# Revit family: PF_ST_RainTrak- O_ACO_2022
name_source: partatom
category: Plumbing Fixtures
units: mm (PartAtom-declared; Revit-internal decimal feet)

## family parameters
Always vertical = No
Cut with Voids When Loaded = Yes
Maintain Annotation Orientation = No
OmniClass Number = 23.70.50.24
OmniClass Title = Rainwater Removal
Part Type = Normal
Room Calculation Point = No
Round Connector Dimension = Use Diameter
Shared = No
Work Plane-Based = Yes

## types (3) — shared parameters
Default Elevation = 1219 mm
Description = Threshold door drainage
Fax = +61 2 4747 4040
IfcDescription = Threshold door drainage
IfcExportAs = IfcWasteTerminalType
IfcExportType = USERDEFINED
Installation guidelines = http://www.acobuildline.com.au
Maintenance guidelines = http://www.acobuildline.com.au
Manufacturer = ACO Pty Ltd
Model = RainTrak
Product_brochure = http://www.acobuildline.com.au
Product_page_URL = http://www.acobuildline.com.au
Telephone = +61 2 4747 4000
URL = www.acobuildline.com.au
d1 = 38 mm
d2 = 51 mm
d3 = 64 mm
d4 = 76 mm
d5 = 89 mm
d6 = 102 mm
region_index = 1

## per-type parameters (varying)
| type | Assembly Code | type_index |
| RainTrak-O-75mm width | D2040300 | 1 |
| RainTrak-O-100mm width |  | 2 |
| RainTrak-O-123mm width |  | 3 |

## geometry (parser evidence)
native form markers: Blend x2, Sweep x6
no freeform markers — native parametric forms only
